# Revit family: Drain_Floor_Heavy_Duty-Zurn-FD2350
name_source: partatom
category: Plumbing Fixtures
units: mm (PartAtom-declared; Revit-internal decimal feet)

## family parameters
Always vertical = Yes
Cut with Voids When Loaded = No
Maintain Annotation Orientation = No
OmniClass Number = 23.45.55.21
OmniClass Title = Drains (Wastes)
Part Type = Normal
Room Calculation Point = No
Round Connector Dimension = Use Radius
Shared = No
Work Plane-Based = No

## types (6) — shared parameters
Assembly Code = D2030300
CW Connection = No
Default Elevation = 25 "
Description = Heavy-Duty Floor Drain
Frame Dimension = 1.938 "
HW Connection = No
Manufacturer = Zurn Water, LLC
Manufacurer Brand = Zurn
Model = FD2350
Modified Date = 11/21/2025
P Trap Primer Connetor = 0.25 "
Product Documentation Link = https://files.zurn.com
Product Page URL = https://www.zurn.com
Product data url = https://www.bimobject.com
Top Diameter = 9 "
URL = www.zurn.com
Vent Connection = No
WFU = 1
Waste Connection = Yes
Width = 11.438 "
zero-valued in all types: CWFU, HWFU

## per-type parameters (varying)
| type | A_ Pipe Size (Actual-Inner) | A_ Pipe Size (Actual-Outer) | A_ Pipe Size (Nominal) | Body | Body Height (D) | Connector Radius | Main Material |
| FD2350-PV2-2 Inch Outlet | 2.067 " | 2.375 " | 2 " | Polyvinyl Chloride - Zurn - Polished | 2.969 " | 1 " | Iron - Zurn - Cast - Painted - Blue |
| FD2350-PV3-3 Inch Outlet | 3.068 " | 3.5 " | 3 " | Polyvinyl Chloride - Zurn - Polished | 3.688 " | 1.5 " | Iron - Zurn - Cast - Painted - Blue |
| FD2350-PV4-4 Inch Outlet | 4.026 " | 4.5 " | 4 " | Polyvinyl Chloride - Zurn - Polished | 3.813 " | 2 " | Iron - Zurn -Cast - Painted - Blue |
| FD2350-AB2-2 Inch Outlet | 2.067 " | 2.375 " | 2 " | Acrylonitrile Butadiene Styrene - Zurn - Polished | 2.969 " | 1 " | Iron - Zurn - Cast - Painted - Blue |
| FD2350-AB3-3 Inch Outlet | 3.068 " | 3.5 " | 3 " | Acrylonitrile Butadiene Styrene - Zurn - Polished | 3.688 " | 1.5 " | Iron - Zurn - Cast - Painted - Blue |
| FD2350-AB4-4 Inch Outlet | 4.026 " | 4.5 " | 4 " | Acrylonitrile Butadiene Styrene - Zurn - Polished | 3.813 " | 2 " | Iron - Zurn -Cast - Painted - Blue |

## geometry (parser evidence)
native form markers: Sweep x4
no freeform markers — native parametric forms only
